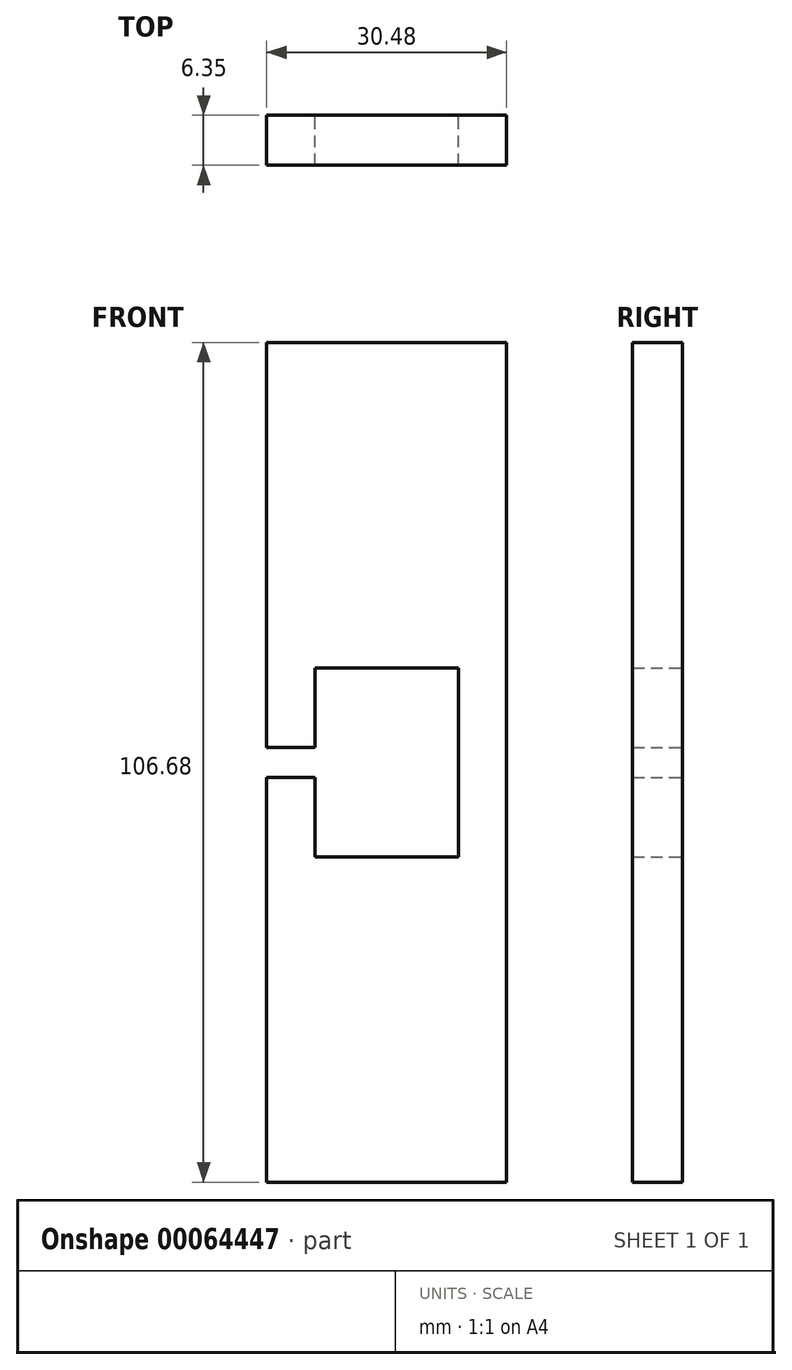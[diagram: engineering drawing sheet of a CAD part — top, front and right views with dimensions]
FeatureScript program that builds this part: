
annotation { "Feature Type Name" : "Feature", "Feature Type Description" : "" }
export const myFeature = defineFeature(function(context is Context, id is Id, definition is map)
    precondition{}
    {
        {
            var Q0;
            Q0=qCreatedBy(makeId("Front.planeOp"),FACE);
            var sketch = newSketch(context, id + "F0", { "sketchPlane" : qUnion([Q0])});
            skLineSegment(sketch, "E0.rect.bottom", {"start": v(15.24, 53.34) * mm, "end": v(-15.24, 53.34) * mm});
            skLineSegment(sketch, "E0.rect.top", {"start": v(15.24, -53.34) * mm, "end": v(-15.24, -53.34) * mm});
            skLineSegment(sketch, "E0.rect.left", {"start": v(15.24, 53.34) * mm, "end": v(15.24, -53.34) * mm});
            skLineSegment(sketch, "E0.rect.right", {"start": v(-15.24, 53.34) * mm, "end": v(-15.24, 1.9) * mm});
            skPoint(sketch, "E0.rect.middle", {"position": v(0, 0) * mm});
            skLineSegment(sketch, "E1.rect.bottom", {"start": v(9.12, 11.99) * mm, "end": v(-9.12, 11.99) * mm});
            skLineSegment(sketch, "E1.rect.top", {"start": v(9.12, -11.99) * mm, "end": v(-9.12, -11.99) * mm});
            skLineSegment(sketch, "E1.rect.left", {"start": v(9.12, 11.99) * mm, "end": v(9.12, -11.99) * mm});
            skLineSegment(sketch, "E1.rect.right", {"start": v(-9.12, 11.99) * mm, "end": v(-9.12, 1.9) * mm});
            skLineSegment(sketch, "E2.bottom", {"start": v(-15.24, 1.9) * mm, "end": v(-9.12, 1.9) * mm});
            skLineSegment(sketch, "E2.top", {"start": v(-15.24, -1.9) * mm, "end": v(-9.12, -1.9) * mm});
            skLineSegment(sketch, "E2.right", {"start": v(15.24, 1.9) * mm, "end": v(15.24, -1.9) * mm});
            skLineSegment(sketch, "E3.trimOffspring", {"start": v(-15.24, -1.9) * mm, "end": v(-15.24, -53.34) * mm});
            skLineSegment(sketch, "E4.trimOffspring", {"start": v(-9.12, -1.9) * mm, "end": v(-9.12, -11.99) * mm});
            skSolve(sketch);
        }
        {
            var Q0;
            Q0 = qSketchRegion(id + "F0", true);
            extrude(context, id + "F1", {"entities" : qUnion([Q0]), "depth" : 6.35 * mm});
        }
    });
